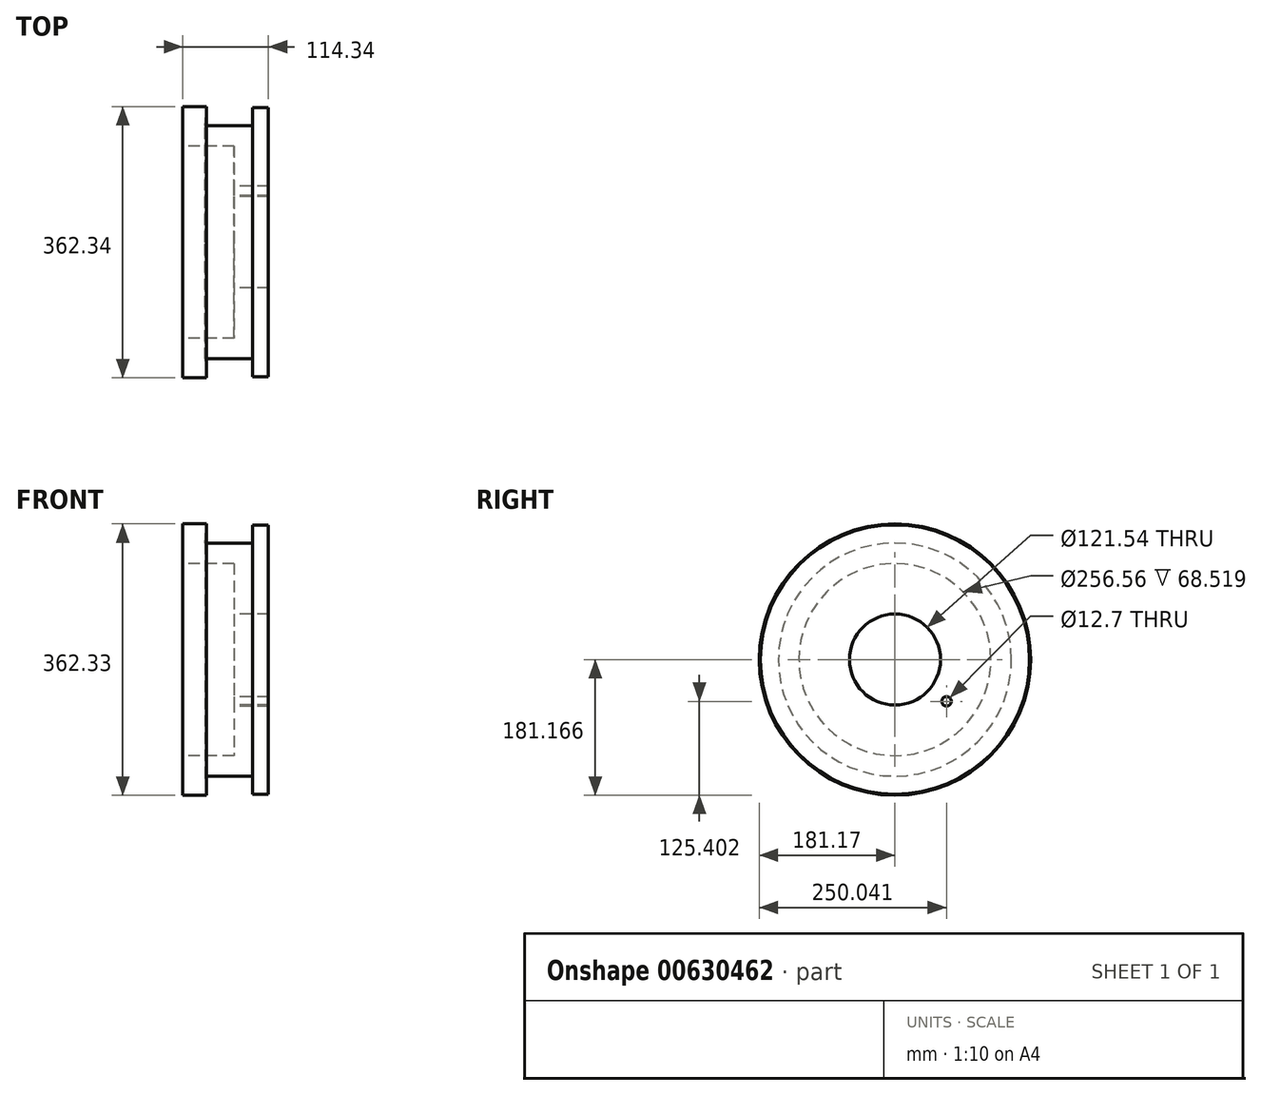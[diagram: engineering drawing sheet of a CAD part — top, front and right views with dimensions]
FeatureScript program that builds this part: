
annotation { "Feature Type Name" : "Feature", "Feature Type Description" : "" }
export const myFeature = defineFeature(function(context is Context, id is Id, definition is map)
    precondition{}
    {
        {
            var Q0;
            Q0=qCreatedBy(makeId("Front.planeOp"),FACE);
            var sketch = newSketch(context, id + "F0", { "sketchPlane" : qUnion([Q0])});
            skLineSegment(sketch, "E0.left", {"start": v(-32.07, 27.33) * mm, "end": v(-32.07, 113.48) * mm});
            skLineSegment(sketch, "E1", {"start": v(-32.07, 27.33) * mm, "end": v(-52.5, 27.33) * mm});
            skLineSegment(sketch, "E2", {"start": v(-52.5, 27.33) * mm, "end": v(-52.5, 94.84) * mm});
            skLineSegment(sketch, "E3", {"start": v(-32.07, 113.48) * mm, "end": v(-32.07, 146.36) * mm});
            skLineSegment(sketch, "E4", {"start": v(-32.07, 146.36) * mm, "end": v(-53.2, 146.36) * mm});
            skLineSegment(sketch, "E5", {"start": v(-53.2, 146.36) * mm, "end": v(-53.2, 122.23) * mm});
            skLineSegment(sketch, "E6", {"start": v(-53.2, 122.23) * mm, "end": v(-116.63, 122.23) * mm});
            skLineSegment(sketch, "E7", {"start": v(-52.5, 94.84) * mm, "end": v(-146.41, 94.84) * mm});
            skLineSegment(sketch, "E8", {"start": v(-146.41, 94.84) * mm, "end": v(-146.41, 147.72) * mm});
            skLineSegment(sketch, "E9", {"start": v(-146.41, 147.72) * mm, "end": v(-114.98, 147.72) * mm});
            skLineSegment(sketch, "E10", {"start": v(-114.98, 147.72) * mm, "end": v(-116.63, 122.23) * mm});
            skSolve(sketch);
        }
        {
            var Q0;
            Q0=qCreatedBy(makeId("Front.planeOp"),FACE);
            var sketch = newSketch(context, id + "F1", { "sketchPlane" : qUnion([Q0])});
            skLineSegment(sketch, "E11", {"start": v(-138.5, -33.44) * mm, "end": v(-21.38, -33.44) * mm});
            skSolve(sketch);
        }
        {
            var Q0;
            Q0=makeQuery(id+"F0.imprint","IMPRINT",FACE,{"disambiguationData":[TD([[makeQuery(id+"F0.imprint","IMPRINT",EDGE,{"derivedFrom":sQuery(id+"F0.wireOp",EDGE,"E0.left")}),1.0]])]});
            var Q1;
            Q1=sQuery(id+"F1.wireOp",EDGE,"E11");
            revolve(context, id + "F2", {"entities" : qUnion([Q0]), "axis" : qUnion([Q1]), "revolveType" : RevolveType.FULL});
        }
        {
            var Q0;
            Q0=makeQuery(id+"F2.opRevolve","SWEPT_FACE",FACE,{"disambiguationData":[OSD([sQuery(id+"F0.wireOp",EDGE,"E2")])]});
            var sketch = newSketch(context, id + "F3", { "sketchPlane" : qUnion([Q0])});
            skPoint(sketch, "E12", {"position": v(-68.87, -89.2) * mm});
            skSolve(sketch);
        }
        {
            var Q0;
            Q0=sQuery(id+"F3.wireOp",VERTEX,"E12");
            var Q1;
            Q1=makeQuery(id+"F2.opRevolve","SWEPT_BODY",BODY,{"disambiguationData":[OSD([sQuery(id+"F0.wireOp",EDGE,"E0.top"),sQuery(id+"F0.wireOp",EDGE,"E0.left"),sQuery(id+"F0.wireOp",EDGE,"E1"),sQuery(id+"F0.wireOp",EDGE,"E2"),sQuery(id+"F0.wireOp",EDGE,"6d1YyYTn-bPER-wdN1-3Jxe-2fQ3ubME4h8t"),sQuery(id+"F0.wireOp",EDGE,"VquT3S6q-QMc1-ul37-hCiW-EYYo1UGuMmfu")])]});
            hole(context, id + "F4", {"style" : HoleStyle.SIMPLE, "endStyle" : HoleEndStyle.THROUGH, "holeDiameter" : 12.7 * mm, "majorDiameter" : 6.35 * mm, "isTappedThrough" : true, "tappedDepth" : 12.7 * mm, "tapClearance" : 3, "locations" : qUnion([Q0]), "scope" : qUnion([Q1])});
        }
        {
            var Q0;
            Q0=makeQuery(id+"F2.opRevolve","SWEPT_FACE",FACE,{"disambiguationData":[OSD([sQuery(id+"F0.wireOp",EDGE,"E2")])]});
            var sketch = newSketch(context, id + "F5", { "sketchPlane" : qUnion([Q0])});
            skSolve(sketch);
        }
        {
            var Q0;
            {var subQ0=sQuery(id+"F0.wireOp",EDGE,"E2");Q0=makeQuery(id+"F5.imprint","IMPRINT",FACE,{"disambiguationData":[TD([[makeQuery(id+"F5.imprint","IMPRINT",EDGE,{"derivedFrom":makeQuery(id+"F2.opRevolve","SWEPT_EDGE",EDGE,{"disambiguationData":[OSD([sQuery(id+"F0.wireOp",EDGE,"E1"),subQ0])]})}),-1.0]])]});}
            extrude(context, id + "F6", {"entities" : qUnion([Q0]), "operationType" : NewBodyOperationType.ADD, "depth" : 25.4 * mm, "offsetDistance" : 25.4 * mm});
        }
    });
